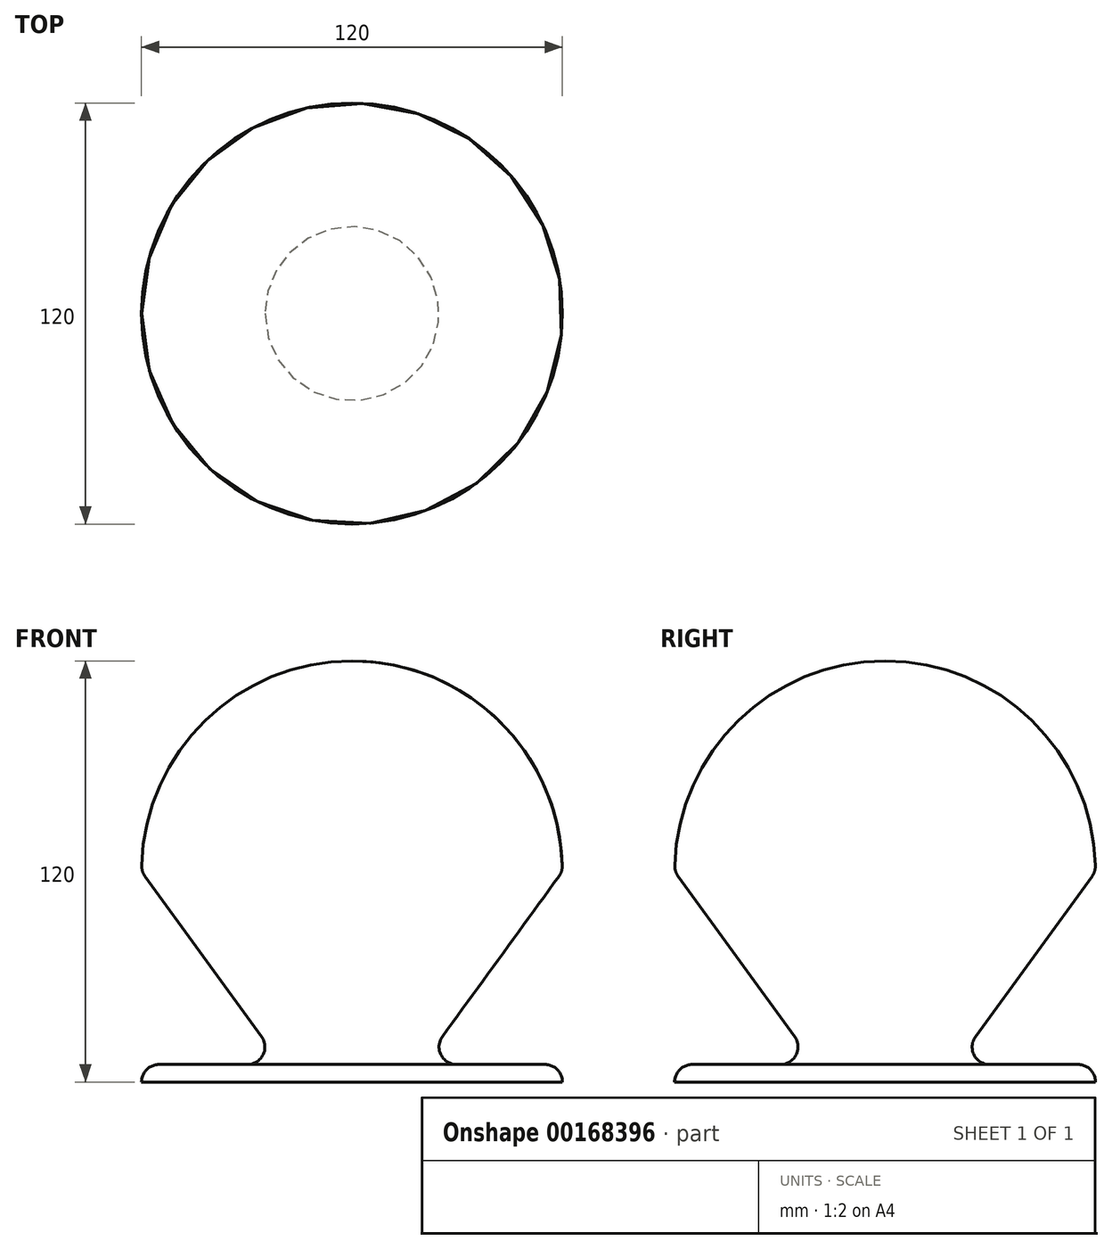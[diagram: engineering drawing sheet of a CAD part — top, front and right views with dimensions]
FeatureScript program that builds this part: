
annotation { "Feature Type Name" : "Feature", "Feature Type Description" : "" }
export const myFeature = defineFeature(function(context is Context, id is Id, definition is map)
    precondition{}
    {
        {
            var Q0;
            Q0=qCreatedBy(makeId("Front.planeOp"),FACE);
            var sketch = newSketch(context, id + "F0", { "sketchPlane" : qUnion([Q0])});
            skLineSegment(sketch, "E0", {"start": v(0, 0) * mm, "end": v(60, 0) * mm});
            skLineSegment(sketch, "E1", {"start": v(60, 0) * mm, "end": v(60, 5) * mm});
            skLineSegment(sketch, "E2", {"start": v(60, 5) * mm, "end": v(20, 5) * mm});
            skLineSegment(sketch, "E3", {"start": v(20, 5) * mm, "end": v(60, 60) * mm});
            skArc(sketch, "E4", {"start": v(60, 60) * mm, "mid": v(42.43, 102.43) * mm, "end": v(0, 120) * mm});
            skLineSegment(sketch, "E5", {"start": v(0, 120) * mm, "end": v(0, 0) * mm});
            skSolve(sketch);
        }
        {
            var Q0;
            Q0 = qSketchRegion(id + "F0", true);
            var Q1;
            Q1=sQuery(id+"F0.wireOp",EDGE,"E5");
            revolve(context, id + "F1", {"entities" : qUnion([Q0]), "axis" : qUnion([Q1]), "revolveType" : RevolveType.FULL});
        }
        {
            var Q0;
            Q0=makeQuery(id+"F1.opRevolve","SWEPT_EDGE",EDGE,{"disambiguationData":[OSD([sQuery(id+"F0.wireOp",EDGE,"E1"),sQuery(id+"F0.wireOp",EDGE,"E2")])]});
            var Q1;
            Q1=makeQuery(id+"F1.opRevolve","SWEPT_EDGE",EDGE,{"disambiguationData":[OSD([sQuery(id+"F0.wireOp",EDGE,"E2"),sQuery(id+"F0.wireOp",EDGE,"E3")])]});
            fillet(context, id + "F2", {"entities" : qUnion([Q0, Q1]), "radius" : 5 * mm, "tangentPropagation" : true, "allowEdgeOverflow" : false});
        }
        {
            var Q0;
            Q0=makeQuery(id+"F1.opRevolve","SWEPT_EDGE",EDGE,{"disambiguationData":[OSD([sQuery(id+"F0.wireOp",EDGE,"E3"),sQuery(id+"F0.wireOp",EDGE,"E4")])]});
            fillet(context, id + "F3", {"entities" : qUnion([Q0]), "radius" : 5 * mm, "tangentPropagation" : true, "allowEdgeOverflow" : false});
        }
    });
